# Revit family: S-tank_HFWT-DUO
name_source: partatom
category: Оборудование
units: mm (PartAtom-declared; Revit-internal decimal feet)

## family parameters
Всегда вертикально = Да
Классификация = Нет
На основе рабочей плоскости = Нет
Общий = Нет
При загрузке вырезать с полостями = Нет
Размер круглого соединителя = Использовать диаметр
Тип детали = Нормальный
Точка расчета площади = Нет

## types (8) — shared parameters
ADSK_URL документации изделия = http://s-tank.ru
ADSK_Группирование = Оборудование
ADSK_Единица измерения = шт.
ADSK_Завод-изготовитель = ООО “С-ТЭНК ВОТЕР ХИТЕРС”
ADSK_Наименование = Буферная емкость c ГВС
DN1 = 40 мм
DN2 = 15 мм
shrf = 18 мм
Разработка семейств = https://rubim.tech

## per-type parameters (varying)
| type | A | ADSK_Код изделия | ADSK_Масса | B | C | D | E | H | I | K | L | M | N | O | P | a | Диаметрсизоляцией |
| HFWT DUO 300 | 125 мм | 2.4002 | 152 | 210 мм | 340 мм | 500 мм | 1040 мм | 1600 мм | 1200 мм | 1360 мм | 210 мм | 430 мм | 570 мм | 1360 мм | 420 мм | 105 мм | 630 мм |
| HFWT DUO 500 | 122 мм | 2.4003 | 170 | 205 мм | 355 мм | 535 мм | 1035 мм | 1680 мм | 1195 мм | 1355 мм | 205 мм | 465 мм | 605 мм | 1355 мм | 445 мм | 130 мм | 780 мм |
| HFWT DUO 750 | 117 мм | 2.4004 | 200 | 195 мм | 345 мм | 575 мм | 1025 мм | 1630 мм | 1185 мм | 1345 мм | 195 мм | 505 мм | 645 мм | 1345 мм | 460 мм | 153 мм | 920 мм |
| HFWT DUO 1000 | 117 мм | 2.4005 | 225 | 195 мм | 440 мм | 865 мм | 1430 мм | 2205 мм | 1675 мм | 1920 мм | 195 мм | 795 мм | 935 мм | 1920 мм | 685 мм | 153 мм | 920 мм |
| HFWT DUO 1200 | 177 мм | 2.4006 | 255 | 265 мм | 455 мм | 965 мм | 1285 мм | 2080 мм | 1475 мм | 1665 мм | 265 мм | 870 мм | 1060 мм | 1665 мм | 645 мм | 178 мм | 1070 мм |
| HFWT DUO 1500 | 177 мм | 2.4007 | 320 | 285 мм | 530 мм | 1142 мм | 1510 мм | 2370 мм | 1755 мм | 2000 мм | 285 мм | 1020 мм | 1265 мм | 2000 мм | 775 мм | 178 мм | 1070 мм |
| HFWT DUO 2000 | 250 мм | 2.4008 | 0 | 350 мм | 540 мм | 1050 мм | 1370 мм | 2100 мм | 1560 мм | 1750 мм | 350 мм | 955 мм | 1145 мм | 1750 мм | 730 мм | 225 мм | 1350 мм |
| HFWT DUO 3000 | 332 мм | 2.4009 | 0 | 465 мм | 655 мм | 1165 мм | 1485 мм | 2315 мм | 1675 мм | 1865 мм | 465 мм | 1070 мм | 1260 мм | 1865 мм | 845 мм | 272 мм | 1630 мм |

note: column(s) folded — value = type name in every type: ADSK_Марка, ADSK_Обозначение
